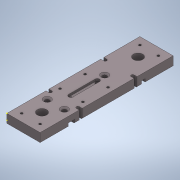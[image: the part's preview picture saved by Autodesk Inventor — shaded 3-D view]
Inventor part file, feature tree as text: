
AUTODESK INVENTOR PART (.ipt)
format: ipt  version: 2021 (Build 250183000, 183)  size: 320,512 bytes
history: native  units: mm
features: sketch x9, hole x6, extrude x5, chamfer x5
ambient origin geometry x8: Origin, YZ Plane, XZ Plane, XY Plane, X Axis, Y Axis, Z Axis, Center Point
bodies: Solid1 (feature_tree)
feature tree (25):
  extrude  "Extrusion1"  Depth=90.0mm
  extrude  "Extrusion2"  Depth=90.0mm
  chamfer  "Chamfer1"  Distance=24.45mm
  extrude  "Extrusion3"  Depth=2.0mm TaperAngle=45.0deg
  hole  "Hole1"  [1 undecoded]
  hole  "Hole2"  [1 undecoded]
  chamfer  "Chamfer3"  Distance=12.5mm
  hole  "Hole3"  [1 undecoded]
  extrude  "Extrusion4"  Depth=3.5mm
  hole  "Hole4"  [1 undecoded]
  chamfer  "Chamfer5"  Distance=9.0mm
  sketch  "Sketch9"  dims[d15=2.5mm d16=0.0mm d17=0.5mm d18=2.0mm d19=45.0deg]
  hole  "Hole5"  [1 undecoded]
  chamfer  "Chamfer6"  Distance=45.1mm
  chamfer  "Chamfer7"  Distance=17.0mm
  extrude  "Extrusion5"  Depth=22.5mm
  hole  "Hole6"  [1 undecoded]
  sketch  "Sketch13"  dims[d41=65.0mm d42=12.5mm d43=6.35mm d44=6.0mm d45=4.0mm d46=2.0mm d47=90.0deg d48=8.0mm d49=20.594885mm d56=2.5mm d57=6.0mm d58=4.0mm d59=2.0mm d60=90.0deg d61=8.0mm d62=20.594885mm d63=0.5mm d64=2.0mm d65=45.0deg d69=3.5mm d70=3.5mm d72=9.0mm d75=1.567mm d76=5.85mm d77=4.0mm d78=2.0mm d79=90.0deg d80=6.3mm d81=20.594885mm d83=1.5mm d84=0.0mm d85=45.1mm d87=17.0mm d88=22.5mm d89=11.89mm d91=3.0mm d92=5.0mm d93=4.0mm d94=2.0mm d95=90.0deg d96=6.3mm d97=20.594885mm d98=1.0mm d99=2.0mm d100=45.0deg d102=11.6mm d103=22.5mm d105=3.0mm d106=5.0mm d107=4.0mm d108=2.0mm d109=90.0deg d110=6.3mm d111=20.594885mm d112=1.0mm d113=2.0mm d114=45.0deg d120=7.0mm d121=10.0mm d123=45.1mm d124=23.45mm d126=2.5mm d127=2.5mm d130=22.5mm d138=0.5mm d139=2.0mm d140=45.0deg d141=2.0mm d142=26.45mm d143=2.0mm d144=2.0mm d145=39.1mm d146=0.0mm d147=0.0mm d148=21.88mm d149=5.45mm d150=22.5mm d151=19.0mm d152=19.0mm d153=32.0mm d154=49.95mm d155=3.0mm d156=55.55mm d157=5.0mm d158=5.0mm d159=5.0mm d160=5.0mm d161=1.567mm d162=4.0mm d163=4.0mm d164=2.0mm d165=90.0deg d166=4.5mm d167=20.594885mm d168=12.5mm d169=80.0mm d170=22.5mm d171=7.5mm d172=7.5mm d174=23.5mm]
  sketch  "Sketch1"  dims[d0=22.5mm d1=90.0mm]
  sketch  "Sketch6"  dims[d2=6.35mm d3=0.0mm d7=90.0mm]
  sketch  "Sketch7"  dims[d9=70.0mm]
  sketch  "Sketch8"  dims[d10=10.0mm d13=41.1mm d14=24.45mm]
  sketch  "Sketch10"  dims[d32=1.5mm d33=2.5mm d34=0.0mm]
  sketch  "Sketch11"  dims[d38=22.5mm d39=90.0mm]
  sketch  "Sketch12"  dims[d40=11.25mm]
note: 6 required parameter values undecoded (feature->parameter linkage not recoverable at this tier; creation-order binding heuristic only, values carry confidence <= 0.55)
